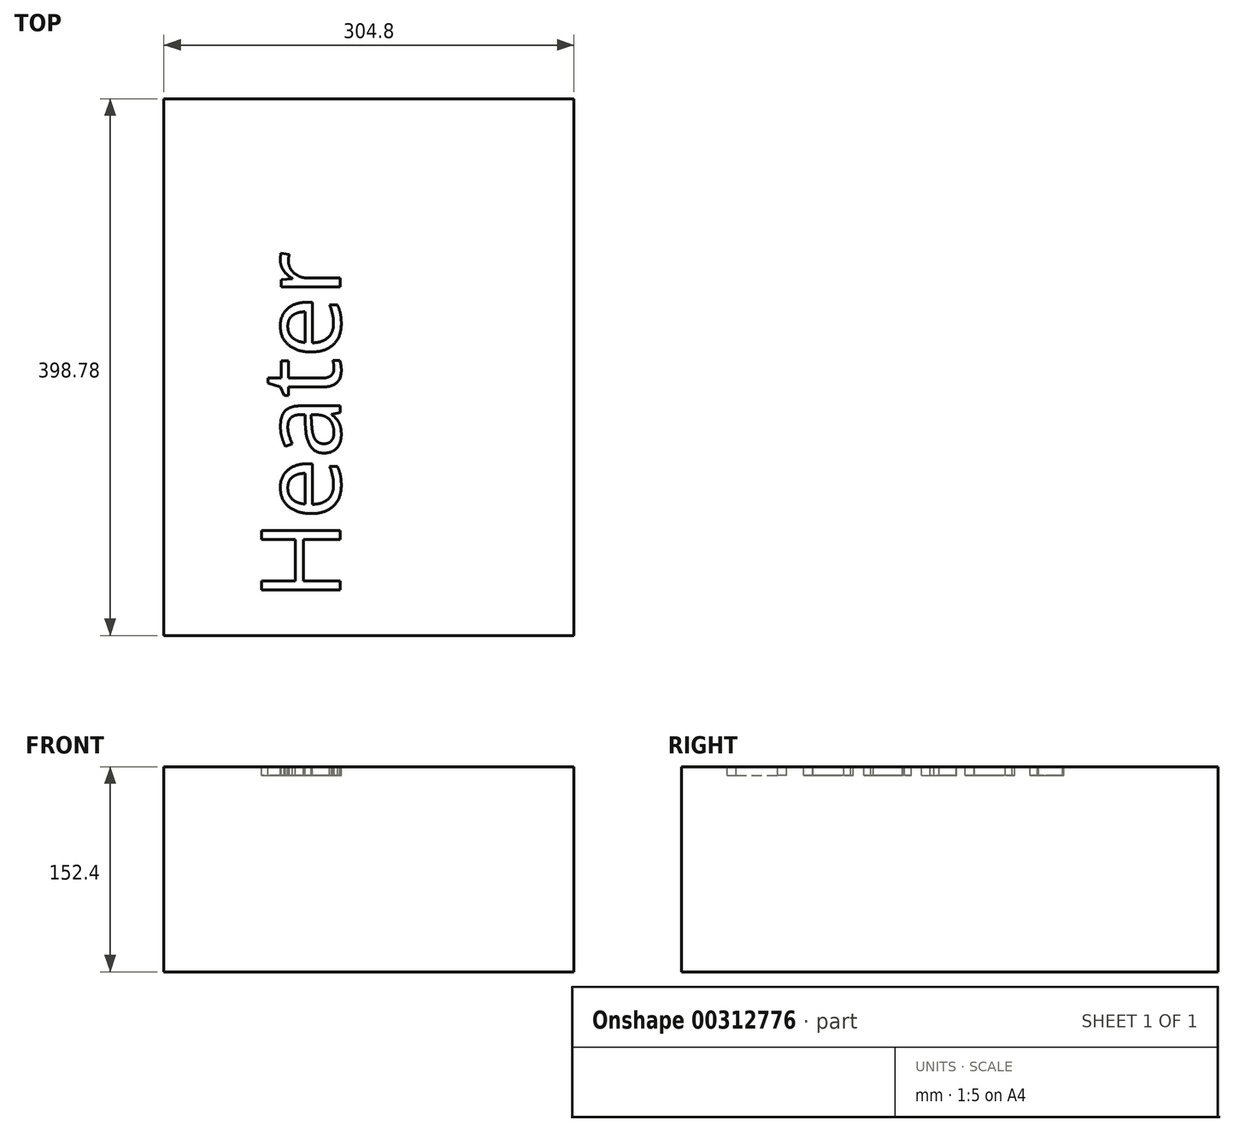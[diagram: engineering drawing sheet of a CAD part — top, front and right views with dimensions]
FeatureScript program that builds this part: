
annotation { "Feature Type Name" : "Feature", "Feature Type Description" : "" }
export const myFeature = defineFeature(function(context is Context, id is Id, definition is map)
    precondition{}
    {
        {
            var Q0;
            Q0=qCreatedBy(makeId("Top.planeOp"),FACE);
            var sketch = newSketch(context, id + "F0", { "sketchPlane" : qUnion([Q0])});
            skLineSegment(sketch, "E0.bottom", {"start": v(0, 0) * mm, "end": v(304.8, 0) * mm});
            skLineSegment(sketch, "E0.top", {"start": v(0, 398.78) * mm, "end": v(304.8, 398.78) * mm});
            skLineSegment(sketch, "E0.left", {"start": v(0, 0) * mm, "end": v(0, 398.78) * mm});
            skLineSegment(sketch, "E0.right", {"start": v(304.8, 0) * mm, "end": v(304.8, 398.78) * mm});
            skSolve(sketch);
        }
        {
            var Q0;
            Q0 = qSketchRegion(id + "F0", true);
            extrude(context, id + "F1", {"entities" : qUnion([Q0]), "depth" : 152.4 * mm});
        }
        {
            var Q0;
            Q0=makeQuery(id+"F1.opExtrude","CAP_FACE",FACE,{"disambiguationData":[OSD([sQuery(id+"F0.wireOp",EDGE,"E0.bottom"),sQuery(id+"F0.wireOp",EDGE,"E0.top"),sQuery(id+"F0.wireOp",EDGE,"E0.left"),sQuery(id+"F0.wireOp",EDGE,"E0.right")])],"isStart":false});
            var sketch = newSketch(context, id + "F2", { "sketchPlane" : qUnion([Q0])});
            skText(sketch, "E1", { "text": "Heater", "fontName": "OpenSans-Regular.ttf"});
            skLineSegment(sketch, "E2", {"start": v(152.4, 398.78) * mm, "end": v(152.4, 331.18) * mm, "construction": true});
            skLineSegment(sketch, "E3", {"start": v(0, 199.4) * mm, "end": v(123, 199.4) * mm, "construction": true});
            const initialGuessF2  = {"E1": [0.131, 0.0257, 0, 1, 0.05879]};
            skSetInitialGuess(sketch, initialGuessF2);
            skSolve(sketch);
        }
        {
            var Q0;
            Q0 = qSketchRegion(id + "F2", true);
            extrude(context, id + "F3", {"entities" : qUnion([Q0]), "operationType" : NewBodyOperationType.REMOVE, "oppositeDirection" : true, "depth" : 6.35 * mm});
        }
    });
